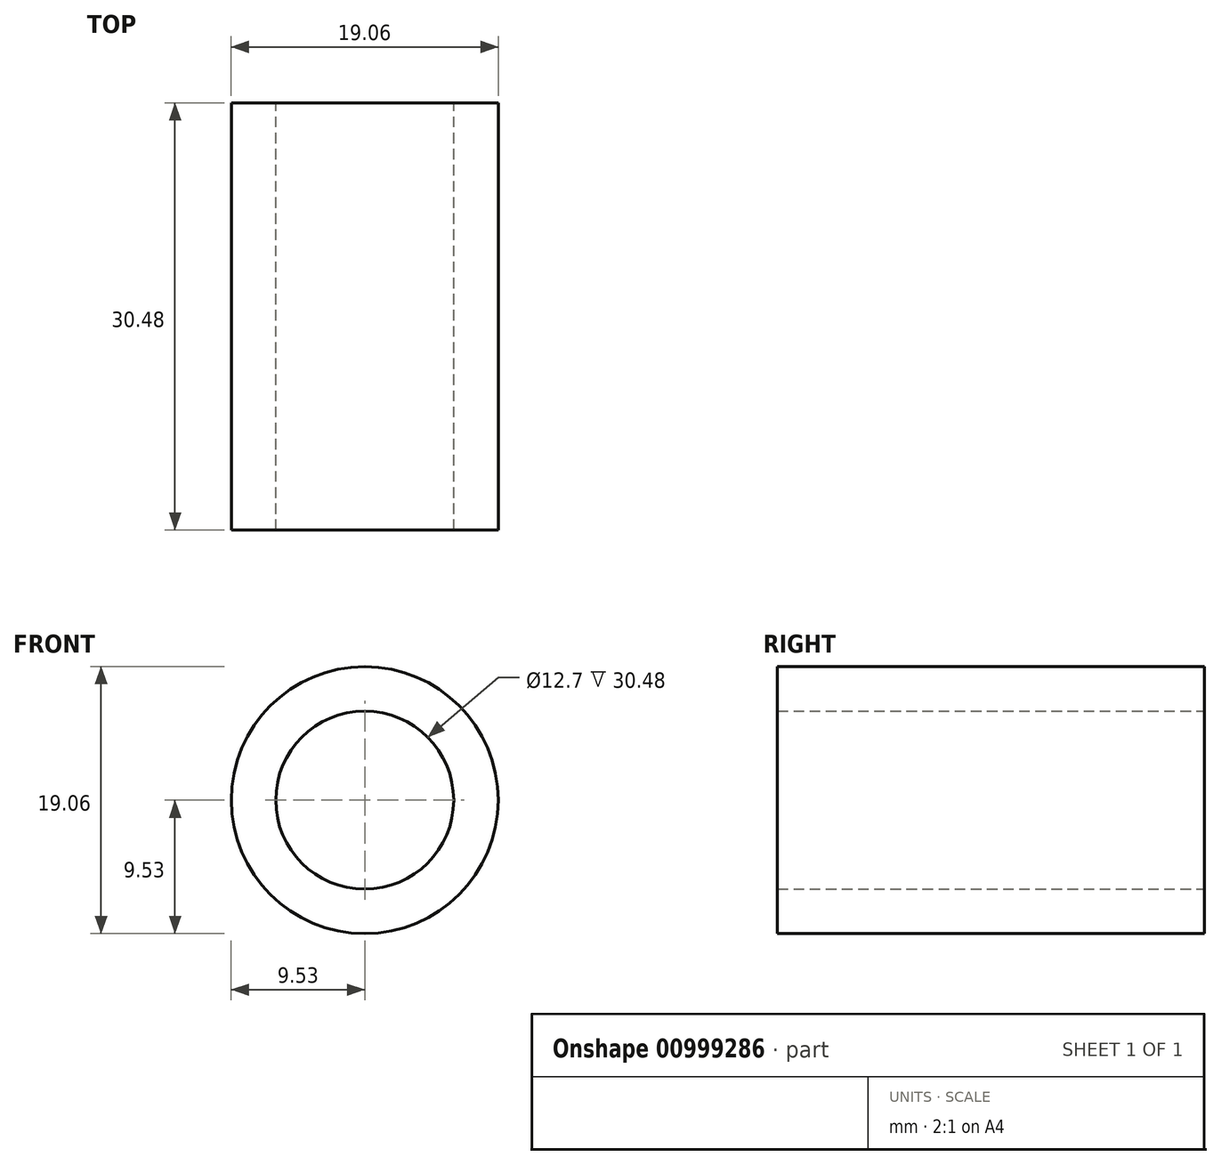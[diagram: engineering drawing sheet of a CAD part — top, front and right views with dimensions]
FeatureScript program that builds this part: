
annotation { "Feature Type Name" : "Feature", "Feature Type Description" : "" }
export const myFeature = defineFeature(function(context is Context, id is Id, definition is map)
    precondition{}
    {
        {
            var Q0;
            Q0=qCreatedBy(makeId("Front.planeOp"),FACE);
            var sketch = newSketch(context, id + "F0", { "sketchPlane" : qUnion([Q0])});
            skCircle(sketch, "E0", {"center": v(0, 0) * mm, "radius": 9.53 * mm});
            skCircle(sketch, "E1", {"center": v(0, 0) * mm, "radius": 6.35 * mm});
            skSolve(sketch);
        }
        {
            var Q0;
            Q0 = qSketchRegion(id + "F0", true);
            extrude(context, id + "F1", {"entities" : qUnion([Q0]), "depth" : 30.48 * mm, "offsetDistance" : 25.4 * mm});
        }
    });
